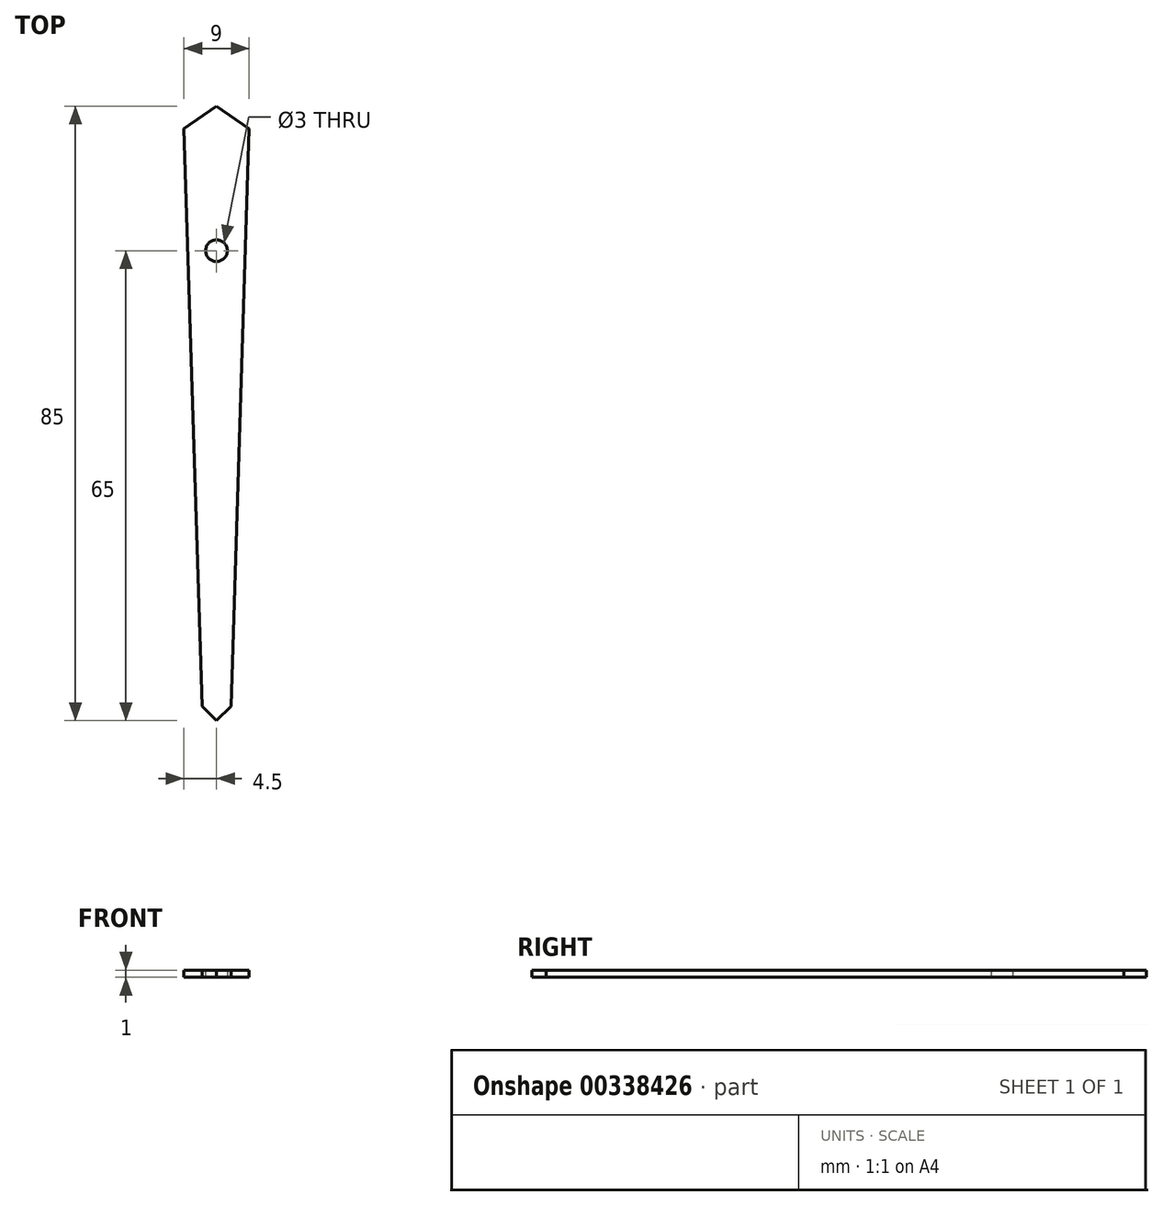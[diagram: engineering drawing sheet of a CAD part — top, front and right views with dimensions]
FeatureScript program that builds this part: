
annotation { "Feature Type Name" : "Feature", "Feature Type Description" : "" }
export const myFeature = defineFeature(function(context is Context, id is Id, definition is map)
    precondition{}
    {
        {
            var Q0;
            Q0=qCreatedBy(makeId("Top.planeOp"),FACE);
            var sketch = newSketch(context, id + "F0", { "sketchPlane" : qUnion([Q0])});
            skCircle(sketch, "E0", {"center": v(0, 0) * mm, "radius": 105 * mm, "construction": true});
            skLineSegment(sketch, "E1", {"start": v(0, 20) * mm, "end": v(0, -65) * mm, "construction": true});
            skLineSegment(sketch, "E2", {"start": v(0, -65) * mm, "end": v(2, -63) * mm});
            skLineSegment(sketch, "E3", {"start": v(0, -65) * mm, "end": v(-2, -63) * mm});
            skLineSegment(sketch, "E4", {"start": v(-2, -63) * mm, "end": v(-4.5, 16.85) * mm});
            skLineSegment(sketch, "E5", {"start": v(-4.5, 16.85) * mm, "end": v(0, 20) * mm});
            skLineSegment(sketch, "E6", {"start": v(0, 20) * mm, "end": v(4.5, 16.85) * mm});
            skLineSegment(sketch, "E7", {"start": v(4.5, 16.85) * mm, "end": v(2, -63) * mm});
            skCircle(sketch, "E8", {"center": v(0, 0) * mm, "radius": 1.5 * mm});
            skCircle(sketch, "E9", {"center": v(0, 0) * mm, "radius": 125 * mm, "construction": true});
            skSolve(sketch);
        }
        {
            var Q0;
            Q0=makeQuery(id+"F0.imprint","IMPRINT",FACE,{"disambiguationData":[TD([[makeQuery(id+"F0.imprint","IMPRINT",EDGE,{"derivedFrom":sQuery(id+"F0.wireOp",EDGE,"E2")}),1.0]])]});
            extrude(context, id + "F1", {"entities" : qUnion([Q0]), "depth" : 1 * mm});
        }
    });
